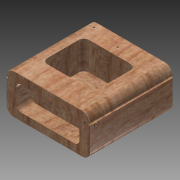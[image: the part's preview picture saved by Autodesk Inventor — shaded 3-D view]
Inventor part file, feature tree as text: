
AUTODESK INVENTOR PART (.ipt)
format: ipt  version: 2015 (Build 190159000, 159)  size: 351,232 bytes
history: native  units: in
note: dims shown in document units (in); Inventor stores cm internally (conversion verified against a paired STEP export)
features: sketch x7, extrude x6, chamfer x4, emboss x1
ambient origin geometry x8: Origin, YZ Plane, XZ Plane, XY Plane, X Axis, Y Axis, Z Axis, Center Point
bodies: Solid1 (feature_tree)
feature tree (18):
  extrude  "Extrusion1"  Depth=3.17in
  extrude  "Extrusion2"  Depth=3.17in TaperAngle=0.0deg
  extrude  "Extrusion3"  Depth=1.59in
  extrude  "Extrusion4"  Depth=0.2in TaperAngle=0.0deg
  extrude  "Extrusion5"  Depth=2.4in
  extrude  "Extrusion6"  Depth=0.3in
  emboss  "Emboss1"
  chamfer  "Chamfer1"  Distance=0.57in
  chamfer  "Chamfer2"  Distance=2.5in
  chamfer  "Chamfer3"  Distance=1.0in
  chamfer  "Chamfer4"  Distance=0.34in
  sketch  "Sketch1"  dims[d0=1.53in d1=3.17in]
  sketch  "Sketch2"  dims[d2=0.3in d3=3.17in d4=0.0in]
  sketch  "Sketch3"  dims[d7=1.98in d8=1.59in]
  sketch  "Sketch4"  dims[d10=0.2in d11=1.07in d12=0.0in]
  sketch  "Sketch5"  dims[d17=0.93in d18=2.4in]
  sketch  "Sketch6"  dims[d19=0.38in d20=0.3in]
  sketch  "Sketch7"  dims[d21=0.2in d22=0.57in d23=0.0in d24=2.5in d25=1.0in d26=0.34in d27=0.26in d28=0.2in d29=0.57in d30=0.0in d31=0.06in d32=3.17in d33=0.06in d34=0.0in d35=0.06in d36=3.17in d37=0.06in d38=0.0in d39=0.02in d40=0.0in d41=0.015in d42=0.125in d43=45.0deg d44=0.015in d45=0.125in d46=45.0deg d47=0.015in d48=0.125in d49=45.0deg d50=0.015in d51=0.125in d52=45.0deg]
